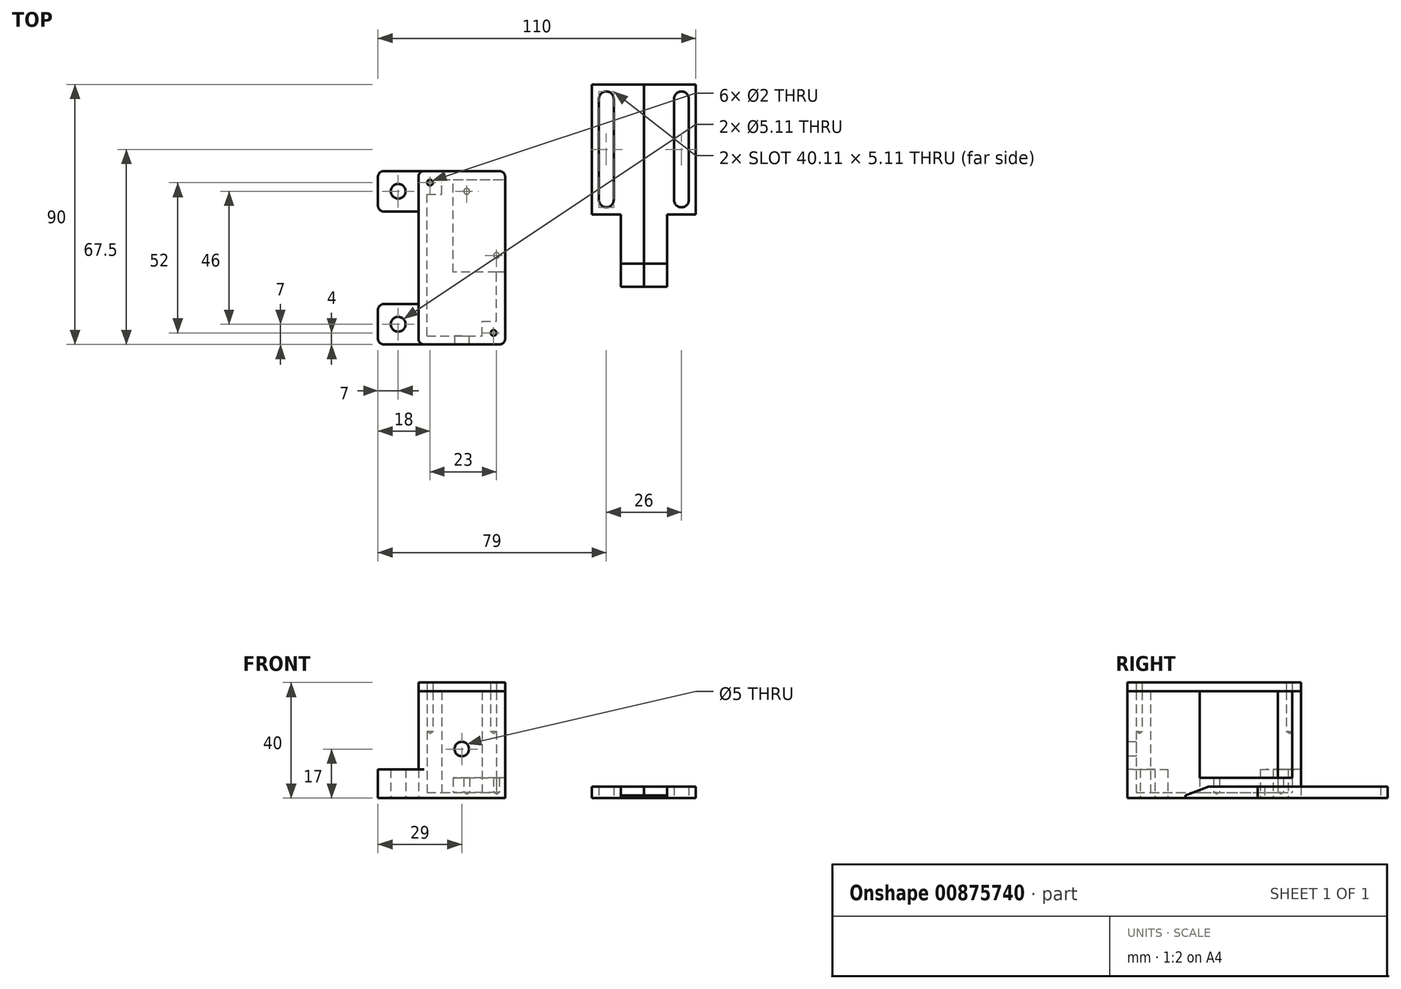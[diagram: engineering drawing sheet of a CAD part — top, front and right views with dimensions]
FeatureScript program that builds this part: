
annotation { "Feature Type Name" : "Feature", "Feature Type Description" : "" }
export const myFeature = defineFeature(function(context is Context, id is Id, definition is map)
    precondition{}
    {
        {
            var Q0;
            Q0=qCreatedBy(makeId("Top.planeOp"),FACE);
            var sketch = newSketch(context, id + "F0", { "sketchPlane" : qUnion([Q0])});
            skLineSegment(sketch, "E0.bottom", {"start": v(0, 0) * mm, "end": v(30, 0) * mm});
            skLineSegment(sketch, "E0.top", {"start": v(0, 60) * mm, "end": v(30, 60) * mm});
            skLineSegment(sketch, "E0.left", {"start": v(0, 0) * mm, "end": v(0, 60) * mm});
            skLineSegment(sketch, "E0.right", {"start": v(30, 0) * mm, "end": v(30, 60) * mm});
            skSolve(sketch);
        }
        {
            var Q0;
            Q0 = qSketchRegion(id + "F0", true);
            extrude(context, id + "F1", {"entities" : qUnion([Q0]), "depth" : 2 * mm, "offsetDistance" : 25 * mm});
        }
        {
            var Q0;
            Q0=makeQuery(id+"F1.opExtrude","CAP_FACE",FACE,{"disambiguationData":[OSD([sQuery(id+"F0.wireOp",EDGE,"E0.bottom"),sQuery(id+"F0.wireOp",EDGE,"E0.top"),sQuery(id+"F0.wireOp",EDGE,"E0.left"),sQuery(id+"F0.wireOp",EDGE,"E0.right")])],"isStart":false});
            var sketch = newSketch(context, id + "F2", { "sketchPlane" : qUnion([Q0])});
            skLineSegment(sketch, "E1.0", {"start": v(0, 60) * mm, "end": v(30, 60) * mm});
            skLineSegment(sketch, "E2.0", {"start": v(0, 0) * mm, "end": v(0, 60) * mm});
            skLineSegment(sketch, "E3.0", {"start": v(30, 0) * mm, "end": v(30, 60) * mm});
            skLineSegment(sketch, "E4.0", {"start": v(3, 57) * mm, "end": v(30, 57) * mm});
            skLineSegment(sketch, "E5.0", {"start": v(3, 3) * mm, "end": v(3, 57) * mm});
            skLineSegment(sketch, "E6.0", {"start": v(3, 3) * mm, "end": v(27, 3) * mm});
            skLineSegment(sketch, "E7.0", {"start": v(27, 3) * mm, "end": v(27, 25) * mm});
            skLineSegment(sketch, "E8.0", {"start": v(0, 0) * mm, "end": v(30, 0) * mm});
            skLineSegment(sketch, "E9", {"start": v(27, 25) * mm, "end": v(30, 25) * mm});
            skLineSegment(sketch, "E10", {"start": v(27, 25) * mm, "end": v(12, 25) * mm});
            skLineSegment(sketch, "E11", {"start": v(12, 25) * mm, "end": v(12, 57) * mm});
            skPoint(sketch, "E12", {"position": v(16.7, 53) * mm});
            skPoint(sketch, "E13", {"position": v(27, 30.8) * mm});
            skSolve(sketch);
        }
        {
            var Q0;
            {var subQ6=sQuery(id+"F2.wireOp",EDGE,"E1.0");Q0=makeQuery(id+"F2.imprint","IMPRINT",FACE,{"disambiguationData":[TD([[makeQuery(id+"F2.imprint","IMPRINT",EDGE,{"derivedFrom":subQ6}),-1.0]])]});}
            extrude(context, id + "F3", {"entities" : qUnion([Q0]), "operationType" : NewBodyOperationType.ADD, "depth" : 35 * mm, "offsetDistance" : 25 * mm});
        }
        {
            var Q0;
            {var subQ0=sQuery(id+"F2.wireOp",EDGE,"E9");Q0=makeQuery(id+"F2.imprint","IMPRINT",FACE,{"disambiguationData":[TD([[makeQuery(id+"F2.imprint","IMPRINT",EDGE,{"derivedFrom":subQ0}),1.0]])]});}
            extrude(context, id + "F4", {"entities" : qUnion([Q0]), "operationType" : NewBodyOperationType.ADD, "depth" : 5 * mm, "offsetDistance" : 25 * mm});
        }
        {
            var Q0;
            Q0=makeQuery(id+"F4.opExtrude","CAP_FACE",FACE,{"disambiguationData":[OSD([sQuery(id+"F2.wireOp",EDGE,"E3.0"),sQuery(id+"F2.wireOp",EDGE,"E4.0"),sQuery(id+"F2.wireOp",EDGE,"E9"),sQuery(id+"F2.wireOp",EDGE,"E10"),sQuery(id+"F2.wireOp",EDGE,"E11")])],"isStart":false});
            var sketch = newSketch(context, id + "F5", { "sketchPlane" : qUnion([Q0])});
            skPoint(sketch, "E14.0", {"position": v(16.7, 53) * mm});
            skPoint(sketch, "E15.0", {"position": v(27, 30.8) * mm});
            skSolve(sketch);
        }
        {
            var Q0;
            Q0=sQuery(id+"F5.wireOp",VERTEX,"E14.0");
            var Q1;
            Q1=sQuery(id+"F5.wireOp",VERTEX,"E15.0");
            var Q2;
            Q2=makeQuery(id+"F1.opExtrude","SWEPT_BODY",BODY,{"disambiguationData":[OSD([sQuery(id+"F0.wireOp",EDGE,"E0.bottom"),sQuery(id+"F0.wireOp",EDGE,"E0.top"),sQuery(id+"F0.wireOp",EDGE,"E0.left"),sQuery(id+"F0.wireOp",EDGE,"E0.right")])]});
            hole(context, id + "F6", {"style" : HoleStyle.SIMPLE, "endStyle" : HoleEndStyle.BLIND, "holeDiameter" : 2 * mm, "majorDiameter" : 5 * mm, "holeDepth" : 5 * mm, "isTappedThrough" : true, "tappedDepth" : 12 * mm, "tapClearance" : 3, "locations" : qUnion([Q0, Q1]), "scope" : qUnion([Q2])});
        }
        {
            var Q0;
            Q0=makeQuery(id+"F3.boolean.opBoolean","MERGE",EDGE,{"derivedFrom":[makeQuery(id+"F1.opExtrude","SWEPT_EDGE",EDGE,{"disambiguationData":[OSD([sQuery(id+"F0.wireOp",EDGE,"E0.bottom"),sQuery(id+"F0.wireOp",EDGE,"E0.right")])]}),makeQuery(id+"F3.opExtrude","SWEPT_EDGE",EDGE,{"disambiguationData":[OSD([sQuery(id+"F2.wireOp",EDGE,"E3.0"),sQuery(id+"F2.wireOp",EDGE,"E8.0")])]})]});
            var Q1;
            Q1=makeQuery(id+"F3.boolean.opBoolean","MERGE",EDGE,{"derivedFrom":[makeQuery(id+"F1.opExtrude","SWEPT_EDGE",EDGE,{"disambiguationData":[OSD([sQuery(id+"F0.wireOp",EDGE,"E0.bottom"),sQuery(id+"F0.wireOp",EDGE,"E0.left")])]}),makeQuery(id+"F3.opExtrude","SWEPT_EDGE",EDGE,{"disambiguationData":[OSD([sQuery(id+"F2.wireOp",EDGE,"E2.0"),sQuery(id+"F2.wireOp",EDGE,"E8.0")])]})]});
            var Q2;
            Q2=makeQuery(id+"F3.boolean.opBoolean","MERGE",EDGE,{"derivedFrom":[makeQuery(id+"F1.opExtrude","SWEPT_EDGE",EDGE,{"disambiguationData":[OSD([sQuery(id+"F0.wireOp",EDGE,"E0.top"),sQuery(id+"F0.wireOp",EDGE,"E0.left")])]}),makeQuery(id+"F3.opExtrude","SWEPT_EDGE",EDGE,{"disambiguationData":[OSD([sQuery(id+"F2.wireOp",EDGE,"E1.0"),sQuery(id+"F2.wireOp",EDGE,"E2.0")])]})]});
            var Q3;
            Q3=makeQuery(id+"F3.boolean.opBoolean","MERGE",EDGE,{"derivedFrom":[makeQuery(id+"F1.opExtrude","SWEPT_EDGE",EDGE,{"disambiguationData":[OSD([sQuery(id+"F0.wireOp",EDGE,"E0.top"),sQuery(id+"F0.wireOp",EDGE,"E0.right")])]}),makeQuery(id+"F3.opExtrude","SWEPT_EDGE",EDGE,{"disambiguationData":[OSD([sQuery(id+"F2.wireOp",EDGE,"E1.0"),sQuery(id+"F2.wireOp",EDGE,"E3.0")])]})]});
            fillet(context, id + "F7", {"entities" : qUnion([Q0, Q1, Q2, Q3]), "tangentPropagation" : true, "radius" : 2 * mm, "defaultsChanged" : false, "vertexSettings" : [], "allowEdgeOverflow" : false});
        }
        {
            var Q0;
            Q0=makeQuery(id+"F1.opExtrude","CAP_FACE",FACE,{"disambiguationData":[OSD([sQuery(id+"F0.wireOp",EDGE,"E0.bottom"),sQuery(id+"F0.wireOp",EDGE,"E0.top"),sQuery(id+"F0.wireOp",EDGE,"E0.left"),sQuery(id+"F0.wireOp",EDGE,"E0.right")])],"isStart":false});
            var sketch = newSketch(context, id + "F8", { "sketchPlane" : qUnion([Q0])});
            skLineSegment(sketch, "E16.0", {"start": v(3, 57) * mm, "end": v(12, 57) * mm});
            skLineSegment(sketch, "E17.0", {"start": v(3, 3) * mm, "end": v(3, 57) * mm});
            skLineSegment(sketch, "E18.0", {"start": v(27, 3) * mm, "end": v(27, 25) * mm});
            skLineSegment(sketch, "E19.0", {"start": v(3, 3) * mm, "end": v(27, 3) * mm});
            skLineSegment(sketch, "E20", {"start": v(3, 52) * mm, "end": v(8, 52) * mm});
            skLineSegment(sketch, "E21", {"start": v(8, 52) * mm, "end": v(8, 57) * mm});
            skLineSegment(sketch, "E22", {"start": v(22, 3) * mm, "end": v(22, 8) * mm});
            skLineSegment(sketch, "E23", {"start": v(22, 8) * mm, "end": v(27, 8) * mm});
            skSolve(sketch);
        }
        {
            var Q0;
            {var subQ4=sQuery(id+"F8.wireOp",EDGE,"E20");Q0=makeQuery(id+"F8.imprint","IMPRINT",FACE,{"disambiguationData":[TD([[makeQuery(id+"F8.imprint","IMPRINT",EDGE,{"derivedFrom":subQ4}),1.0]])]});}
            var Q1;
            {var subQ4=sQuery(id+"F8.wireOp",EDGE,"E22");Q1=makeQuery(id+"F8.imprint","IMPRINT",FACE,{"disambiguationData":[TD([[makeQuery(id+"F8.imprint","IMPRINT",EDGE,{"derivedFrom":subQ4}),-1.0]])]});}
            var Q2;
            Q2=makeQuery(id+"F3.opExtrude","CAP_FACE",FACE,{"disambiguationData":[OSD([sQuery(id+"F2.wireOp",EDGE,"E1.0"),sQuery(id+"F2.wireOp",EDGE,"E2.0"),sQuery(id+"F2.wireOp",EDGE,"E3.0"),sQuery(id+"F2.wireOp",EDGE,"E4.0"),sQuery(id+"F2.wireOp",EDGE,"E5.0"),sQuery(id+"F2.wireOp",EDGE,"E6.0"),sQuery(id+"F2.wireOp",EDGE,"E7.0"),sQuery(id+"F2.wireOp",EDGE,"E8.0"),sQuery(id+"F2.wireOp",EDGE,"E9")])],"isStart":false});
            extrude(context, id + "F9", {"entities" : qUnion([Q0, Q1]), "operationType" : NewBodyOperationType.ADD, "endBound" : BoundingType.UP_TO_SURFACE, "depth" : 25 * mm, "endBoundEntityFace" : qUnion([Q2]), "offsetDistance" : 25 * mm});
        }
        {
            var Q0;
            Q0=makeQuery(id+"F9.boolean.opBoolean","MERGE",FACE,{"derivedFrom":[makeQuery(id+"F3.opExtrude","CAP_FACE",FACE,{"disambiguationData":[OSD([sQuery(id+"F2.wireOp",EDGE,"E1.0"),sQuery(id+"F2.wireOp",EDGE,"E2.0"),sQuery(id+"F2.wireOp",EDGE,"E3.0"),sQuery(id+"F2.wireOp",EDGE,"E4.0"),sQuery(id+"F2.wireOp",EDGE,"E5.0"),sQuery(id+"F2.wireOp",EDGE,"E6.0"),sQuery(id+"F2.wireOp",EDGE,"E7.0"),sQuery(id+"F2.wireOp",EDGE,"E8.0"),sQuery(id+"F2.wireOp",EDGE,"E9")])],"isStart":false}),makeQuery(id+"F9.opExtrude","CAP_FACE",FACE,{"disambiguationData":[OSD([sQuery(id+"F8.wireOp",EDGE,"E16.0"),sQuery(id+"F8.wireOp",EDGE,"E17.0"),sQuery(id+"F8.wireOp",EDGE,"E20"),sQuery(id+"F8.wireOp",EDGE,"E21")])],"isStart":false}),makeQuery(id+"F9.opExtrude","CAP_FACE",FACE,{"disambiguationData":[OSD([sQuery(id+"F8.wireOp",EDGE,"E18.0"),sQuery(id+"F8.wireOp",EDGE,"E19.0"),sQuery(id+"F8.wireOp",EDGE,"E22"),sQuery(id+"F8.wireOp",EDGE,"E23")])],"isStart":false})]});
            var sketch = newSketch(context, id + "F10", { "sketchPlane" : qUnion([Q0])});
            skPoint(sketch, "E24", {"position": v(4, 56) * mm});
            skPoint(sketch, "E25", {"position": v(26, 4) * mm});
            skSolve(sketch);
        }
        {
            var Q0;
            Q0=sQuery(id+"F10.wireOp",VERTEX,"E24");
            var Q1;
            Q1=sQuery(id+"F10.wireOp",VERTEX,"E25");
            var Q2;
            Q2=makeQuery(id+"F1.opExtrude","SWEPT_BODY",BODY,{"disambiguationData":[OSD([sQuery(id+"F0.wireOp",EDGE,"E0.bottom"),sQuery(id+"F0.wireOp",EDGE,"E0.top"),sQuery(id+"F0.wireOp",EDGE,"E0.left"),sQuery(id+"F0.wireOp",EDGE,"E0.right")])]});
            hole(context, id + "F11", {"style" : HoleStyle.SIMPLE, "endStyle" : HoleEndStyle.BLIND, "holeDiameter" : 2 * mm, "majorDiameter" : 5 * mm, "holeDepth" : 14 * mm, "isTappedThrough" : true, "tappedDepth" : 12 * mm, "tapClearance" : 3, "locations" : qUnion([Q0, Q1]), "scope" : qUnion([Q2])});
        }
        {
            var Q0;
            Q0=makeQuery(id+"F3.boolean.opBoolean","MERGE",FACE,{"derivedFrom":[makeQuery(id+"F1.opExtrude","SWEPT_FACE",FACE,{"disambiguationData":[OSD([sQuery(id+"F0.wireOp",EDGE,"E0.bottom")])]}),makeQuery(id+"F3.opExtrude","SWEPT_FACE",FACE,{"disambiguationData":[OSD([sQuery(id+"F2.wireOp",EDGE,"E8.0")])]})]});
            var sketch = newSketch(context, id + "F12", { "sketchPlane" : qUnion([Q0])});
            skCircle(sketch, "E26", {"center": v(15, 17) * mm, "radius": 2.5 * mm});
            skPoint(sketch, "E27.0", {"position": v(15, 0) * mm});
            skLineSegment(sketch, "E28.0", {"start": v(27, 7) * mm, "end": v(12, 7) * mm});
            skSolve(sketch);
        }
        {
            var Q0;
            Q0=makeQuery(id+"F12.imprint","IMPRINT",FACE,{"disambiguationData":[TD([[makeQuery(id+"F12.imprint","IMPRINT",EDGE,{"derivedFrom":sQuery(id+"F12.wireOp",EDGE,"E26")}),1.0]])]});
            extrude(context, id + "F13", {"entities" : qUnion([Q0]), "operationType" : NewBodyOperationType.REMOVE, "endBound" : BoundingType.UP_TO_NEXT, "oppositeDirection" : true, "depth" : 25 * mm, "offsetDistance" : 25 * mm});
        }
        {
            var Q0;
            Q0=makeQuery(id+"F1.opExtrude","CAP_FACE",FACE,{"disambiguationData":[OSD([sQuery(id+"F0.wireOp",EDGE,"E0.bottom"),sQuery(id+"F0.wireOp",EDGE,"E0.top"),sQuery(id+"F0.wireOp",EDGE,"E0.left"),sQuery(id+"F0.wireOp",EDGE,"E0.right")])],"isStart":true});
            var sketch = newSketch(context, id + "F14", { "sketchPlane" : qUnion([Q0])});
            skLineSegment(sketch, "E29", {"start": v(2, 0) * mm, "end": v(-14, 0) * mm});
            skLineSegment(sketch, "E30", {"start": v(-14, 0) * mm, "end": v(-14, -14) * mm});
            skLineSegment(sketch, "E31", {"start": v(-14, -14) * mm, "end": v(0, -14) * mm});
            skLineSegment(sketch, "E32", {"start": v(2, -60) * mm, "end": v(-14, -60) * mm});
            skLineSegment(sketch, "E33", {"start": v(-14, -60) * mm, "end": v(-14, -46) * mm});
            skLineSegment(sketch, "E34", {"start": v(-14, -46) * mm, "end": v(0, -46) * mm});
            skSolve(sketch);
        }
        {
            var Q0;
            Q0=makeQuery(id+"F14.imprint","IMPRINT",FACE,{"disambiguationData":[TD([[makeQuery(id+"F14.imprint","IMPRINT",EDGE,{"derivedFrom":sQuery(id+"F14.wireOp",EDGE,"E32")}),-1.0]])]});
            var Q1;
            Q1=makeQuery(id+"F14.imprint","IMPRINT",FACE,{"disambiguationData":[TD([[makeQuery(id+"F14.imprint","IMPRINT",EDGE,{"derivedFrom":sQuery(id+"F14.wireOp",EDGE,"E29")}),1.0]])]});
            extrude(context, id + "F15", {"entities" : qUnion([Q0, Q1]), "operationType" : NewBodyOperationType.ADD, "oppositeDirection" : true, "depth" : 10 * mm, "offsetDistance" : 25 * mm});
        }
        {
            var Q0;
            Q0=makeQuery(id+"F15.opExtrude","CAP_FACE",FACE,{"disambiguationData":[OSD([sQuery(id+"F0.wireOp",EDGE,"E0.bottom"),sQuery(id+"F0.wireOp",EDGE,"E0.top"),sQuery(id+"F0.wireOp",EDGE,"E0.left"),sQuery(id+"F0.wireOp",EDGE,"E0.right"),sQuery(id+"F2.wireOp",EDGE,"E2.0"),sQuery(id+"F2.wireOp",EDGE,"E8.0"),sQuery(id+"F14.wireOp",EDGE,"E29"),sQuery(id+"F14.wireOp",EDGE,"E30"),sQuery(id+"F14.wireOp",EDGE,"E31")])],"isStart":false});
            var sketch = newSketch(context, id + "F16", { "sketchPlane" : qUnion([Q0])});
            skPoint(sketch, "E35", {"position": v(-7, 7) * mm});
            skPoint(sketch, "E36", {"position": v(-7, 53) * mm});
            skSolve(sketch);
        }
        {
            var Q0;
            Q0=sQuery(id+"F16.wireOp",VERTEX,"E36");
            var Q1;
            Q1=sQuery(id+"F16.wireOp",VERTEX,"E35");
            var Q2;
            Q2=makeQuery(id+"F1.opExtrude","SWEPT_BODY",BODY,{"disambiguationData":[OSD([sQuery(id+"F0.wireOp",EDGE,"E0.bottom"),sQuery(id+"F0.wireOp",EDGE,"E0.top"),sQuery(id+"F0.wireOp",EDGE,"E0.left"),sQuery(id+"F0.wireOp",EDGE,"E0.right")])]});
            hole(context, id + "F17", {"style" : HoleStyle.SIMPLE, "endStyle" : HoleEndStyle.THROUGH, "standardTappedOrClearance" : lookupTablePath({ "fit" : "Free", "standard" : "ANSI", "size" : "#10", "type" : "Clearance" }), "standardBlindInLast" : lookupTablePath({ "fit" : "Free", "standard" : "ANSI", "engagement" : "75%", "pitch" : "24 tpi", "size" : "#10", "type" : "Clearance & tapped" }), "holeDiameter" : 5.1 * mm, "majorDiameter" : 4.83 * mm, "isTappedThrough" : true, "tappedDepth" : 12 * mm, "tapClearance" : 3, "locations" : qUnion([Q0, Q1]), "scope" : qUnion([Q2])});
        }
        {
            var Q0;
            Q0=makeQuery(id+"F15.opExtrude","SWEPT_EDGE",EDGE,{"disambiguationData":[OSD([sQuery(id+"F14.wireOp",EDGE,"E33"),sQuery(id+"F14.wireOp",EDGE,"E34")])]});
            var Q1;
            Q1=makeQuery(id+"F15.opExtrude","SWEPT_EDGE",EDGE,{"disambiguationData":[OSD([sQuery(id+"F14.wireOp",EDGE,"E32"),sQuery(id+"F14.wireOp",EDGE,"E33")])]});
            var Q2;
            Q2=makeQuery(id+"F15.opExtrude","SWEPT_EDGE",EDGE,{"disambiguationData":[OSD([sQuery(id+"F14.wireOp",EDGE,"E29"),sQuery(id+"F14.wireOp",EDGE,"E30")])]});
            var Q3;
            Q3=makeQuery(id+"F15.opExtrude","SWEPT_EDGE",EDGE,{"disambiguationData":[OSD([sQuery(id+"F14.wireOp",EDGE,"E30"),sQuery(id+"F14.wireOp",EDGE,"E31")])]});
            var Q4;
            Q4=makeQuery(id+"F15.opExtrude","SWEPT_EDGE",EDGE,{"disambiguationData":[OSD([sQuery(id+"F0.wireOp",EDGE,"E0.left"),sQuery(id+"F14.wireOp",EDGE,"E34")])]});
            var Q5;
            Q5=makeQuery(id+"F15.opExtrude","SWEPT_EDGE",EDGE,{"disambiguationData":[OSD([sQuery(id+"F0.wireOp",EDGE,"E0.left"),sQuery(id+"F14.wireOp",EDGE,"E31")])]});
            var Q6;
            {var subQ0=sQuery(id+"F0.wireOp",EDGE,"E0.left");var subQ2=makeQuery(id+"F1.opExtrude","CAP_EDGE",EDGE,{"disambiguationData":[OSD([subQ0])],"isStart":true});Q6=makeQuery(id+"F15.opExtrude","CAP_EDGE",EDGE,{"disambiguationData":[OSD([subQ0]),TDD([makeQuery(id+"F14.imprint","IMPRINT",EDGE,{"disambiguationData":[TD([[makeQuery(id+"F14.imprint","INTERSECT",VERTEX,{"derivedFrom":[subQ2,sQuery(id+"F14.wireOp",EDGE,"E31")]}),1.0]])],"derivedFrom":subQ2})])],"isStart":false});}
            var Q7;
            {var subQ0=sQuery(id+"F0.wireOp",EDGE,"E0.left");var subQ2=makeQuery(id+"F1.opExtrude","CAP_EDGE",EDGE,{"disambiguationData":[OSD([subQ0])],"isStart":true});Q7=makeQuery(id+"F15.opExtrude","CAP_EDGE",EDGE,{"disambiguationData":[OSD([subQ0]),TDD([makeQuery(id+"F14.imprint","IMPRINT",EDGE,{"disambiguationData":[TD([[makeQuery(id+"F14.imprint","INTERSECT",VERTEX,{"derivedFrom":[subQ2,sQuery(id+"F14.wireOp",EDGE,"E34")]}),-1.0]])],"derivedFrom":subQ2})])],"isStart":false});}
            fillet(context, id + "F18", {"entities" : qUnion([Q0, Q1, Q2, Q3, Q4, Q5, Q6, Q7]), "tangentPropagation" : true, "radius" : 2 * mm, "defaultsChanged" : false, "vertexSettings" : [], "allowEdgeOverflow" : false});
        }
        {
            var Q0;
            Q0=makeQuery(id+"F9.boolean.opBoolean","MERGE",FACE,{"derivedFrom":[makeQuery(id+"F3.opExtrude","CAP_FACE",FACE,{"disambiguationData":[OSD([sQuery(id+"F2.wireOp",EDGE,"E1.0"),sQuery(id+"F2.wireOp",EDGE,"E2.0"),sQuery(id+"F2.wireOp",EDGE,"E3.0"),sQuery(id+"F2.wireOp",EDGE,"E4.0"),sQuery(id+"F2.wireOp",EDGE,"E5.0"),sQuery(id+"F2.wireOp",EDGE,"E6.0"),sQuery(id+"F2.wireOp",EDGE,"E7.0"),sQuery(id+"F2.wireOp",EDGE,"E8.0"),sQuery(id+"F2.wireOp",EDGE,"E9")])],"isStart":false}),makeQuery(id+"F9.opExtrude","CAP_FACE",FACE,{"disambiguationData":[OSD([sQuery(id+"F8.wireOp",EDGE,"E16.0"),sQuery(id+"F8.wireOp",EDGE,"E17.0"),sQuery(id+"F8.wireOp",EDGE,"E20"),sQuery(id+"F8.wireOp",EDGE,"E21")])],"isStart":false}),makeQuery(id+"F9.opExtrude","CAP_FACE",FACE,{"disambiguationData":[OSD([sQuery(id+"F8.wireOp",EDGE,"E18.0"),sQuery(id+"F8.wireOp",EDGE,"E19.0"),sQuery(id+"F8.wireOp",EDGE,"E22"),sQuery(id+"F8.wireOp",EDGE,"E23")])],"isStart":false})]});
            var sketch = newSketch(context, id + "F19", { "sketchPlane" : qUnion([Q0])});
            skLineSegment(sketch, "E37", {"start": v(30, 25) * mm, "end": v(30, 57) * mm});
            skSolve(sketch);
        }
        {
            var Q0;
            {var subQ3=sQuery(id+"F2.wireOp",EDGE,"E9");Q0=makeQuery(id+"F19.imprint","IMPRINT",FACE,{"disambiguationData":[TD([[makeQuery(id+"F19.imprint","IMPRINT",EDGE,{"derivedFrom":makeQuery(id+"F3.opExtrude","CAP_EDGE",EDGE,{"disambiguationData":[OSD([subQ3])],"isStart":false})}),-1.0]])]});}
            var Q1;
            Q1=makeQuery(id+"F19.imprint","IMPRINT",FACE,{"disambiguationData":[TD([[makeQuery(id+"F19.imprint","IMPRINT",EDGE,{"derivedFrom":sQuery(id+"F19.wireOp",EDGE,"E37")}),1.0]])]});
            extrude(context, id + "F20", {"entities" : qUnion([Q0, Q1]), "depth" : 3 * mm, "offsetDistance" : 25 * mm});
        }
        {
            var Q0;
            Q0=qCreatedBy(makeId("Top.planeOp"),FACE);
            var sketch = newSketch(context, id + "F21", { "sketchPlane" : qUnion([Q0])});
            skLineSegment(sketch, "E38.bottom", {"start": v(60, 20) * mm, "end": v(78, 20) * mm});
            skLineSegment(sketch, "E38.top", {"start": v(60, 90) * mm, "end": v(78, 90) * mm});
            skLineSegment(sketch, "E38.left", {"start": v(60, 20) * mm, "end": v(60, 90) * mm});
            skLineSegment(sketch, "E38.right", {"start": v(78, 20) * mm, "end": v(78, 90) * mm});
            skArc(sketch, "E39", {"start": v(67.55, 85) * mm, "mid": v(65, 87.55) * mm, "end": v(62.45, 85) * mm});
            skArc(sketch, "E40", {"start": v(62.45, 50) * mm, "mid": v(65, 47.45) * mm, "end": v(67.55, 50) * mm});
            skLineSegment(sketch, "E41", {"start": v(62.45, 85) * mm, "end": v(62.45, 50) * mm});
            skLineSegment(sketch, "E42", {"start": v(67.55, 85) * mm, "end": v(67.55, 50) * mm});
            skLineSegment(sketch, "E43", {"start": v(60, 45) * mm, "end": v(70, 45) * mm});
            skLineSegment(sketch, "E44", {"start": v(70, 45) * mm, "end": v(70, 20) * mm});
            skSolve(sketch);
        }
        {
            var Q0;
            {var subQ2=sQuery(id+"F21.wireOp",EDGE,"E38.top");Q0=makeQuery(id+"F21.imprint","IMPRINT",FACE,{"disambiguationData":[TD([[makeQuery(id+"F21.imprint","IMPRINT",EDGE,{"derivedFrom":subQ2}),-1.0]])]});}
            extrude(context, id + "F22", {"entities" : qUnion([Q0]), "depth" : 4 * mm, "offsetDistance" : 25 * mm});
        }
        {
            var Q0;
            Q0=makeQuery(id+"F22.opExtrude","CAP_EDGE",EDGE,{"disambiguationData":[OSD([sQuery(id+"F21.wireOp",EDGE,"E38.bottom")])],"isStart":false});
            chamfer(context, id + "F23", {"entities" : qUnion([Q0]), "chamferType" : ChamferType.TWO_OFFSETS, "width1" : 8 * mm, "oppositeDirection" : false, "width2" : 3 * mm, "tangentPropagation" : true});
        }
        {
            var Q0;
            Q0=makeQuery(id+"F22.opExtrude","SWEPT_BODY",BODY,{"disambiguationData":[OSD([sQuery(id+"F21.wireOp",EDGE,"E38.bottom"),sQuery(id+"F21.wireOp",EDGE,"E38.top"),sQuery(id+"F21.wireOp",EDGE,"E38.left"),sQuery(id+"F21.wireOp",EDGE,"E38.right"),sQuery(id+"F21.wireOp",EDGE,"E39"),sQuery(id+"F21.wireOp",EDGE,"E40"),sQuery(id+"F21.wireOp",EDGE,"E41"),sQuery(id+"F21.wireOp",EDGE,"E42")])]});
            var Q1;
            Q1=makeQuery(id+"F22.opExtrude","SWEPT_FACE",FACE,{"disambiguationData":[OSD([sQuery(id+"F21.wireOp",EDGE,"E38.right")])]});
            mirror(context, id + "F24", {"entities" : qUnion([Q0]), "mirrorPlane" : qUnion([Q1])});
        }
    });
